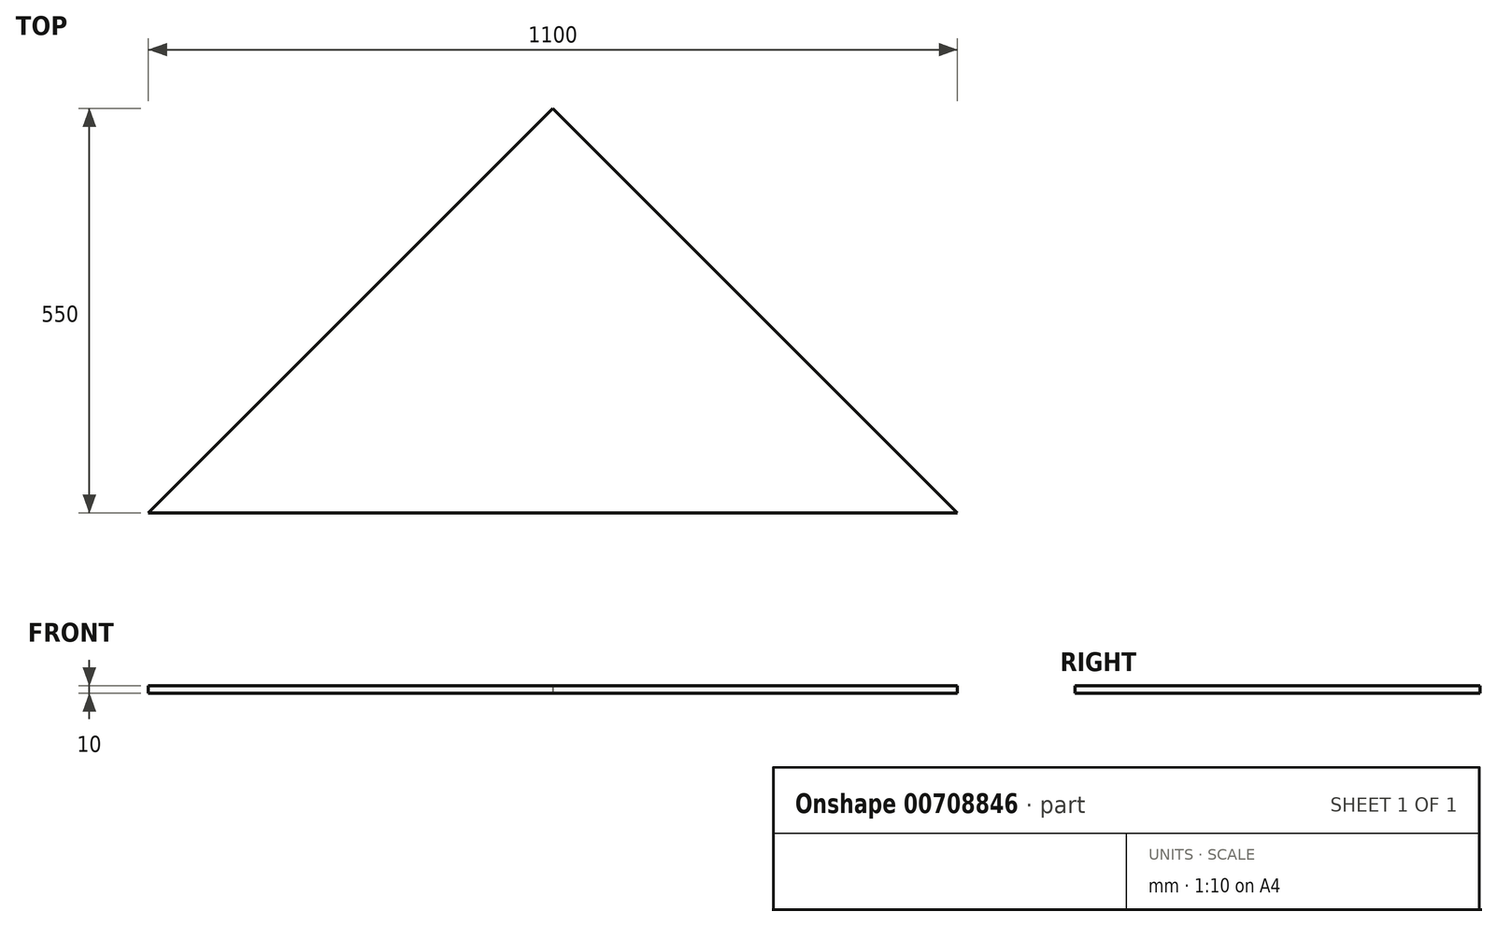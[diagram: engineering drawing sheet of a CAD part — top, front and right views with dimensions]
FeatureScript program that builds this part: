
annotation { "Feature Type Name" : "Feature", "Feature Type Description" : "" }
export const myFeature = defineFeature(function(context is Context, id is Id, definition is map)
    precondition{}
    {
        {
            var Q0;
            Q0=qCreatedBy(makeId("Top.planeOp"),FACE);
            var sketch = newSketch(context, id + "F0", { "sketchPlane" : qUnion([Q0])});
            skLineSegment(sketch, "E0", {"start": v(-550, 0) * mm, "end": v(550, 0) * mm});
            skLineSegment(sketch, "E1", {"start": v(550, 0) * mm, "end": v(0, 550) * mm});
            skLineSegment(sketch, "E2", {"start": v(0, 550) * mm, "end": v(-550, 0) * mm});
            skSolve(sketch);
        }
        {
            var Q0;
            Q0 = qSketchRegion(id + "F0", true);
            extrude(context, id + "F1", {"entities" : qUnion([Q0]), "depth" : 10 * mm, "offsetDistance" : 25 * mm});
        }
    });
